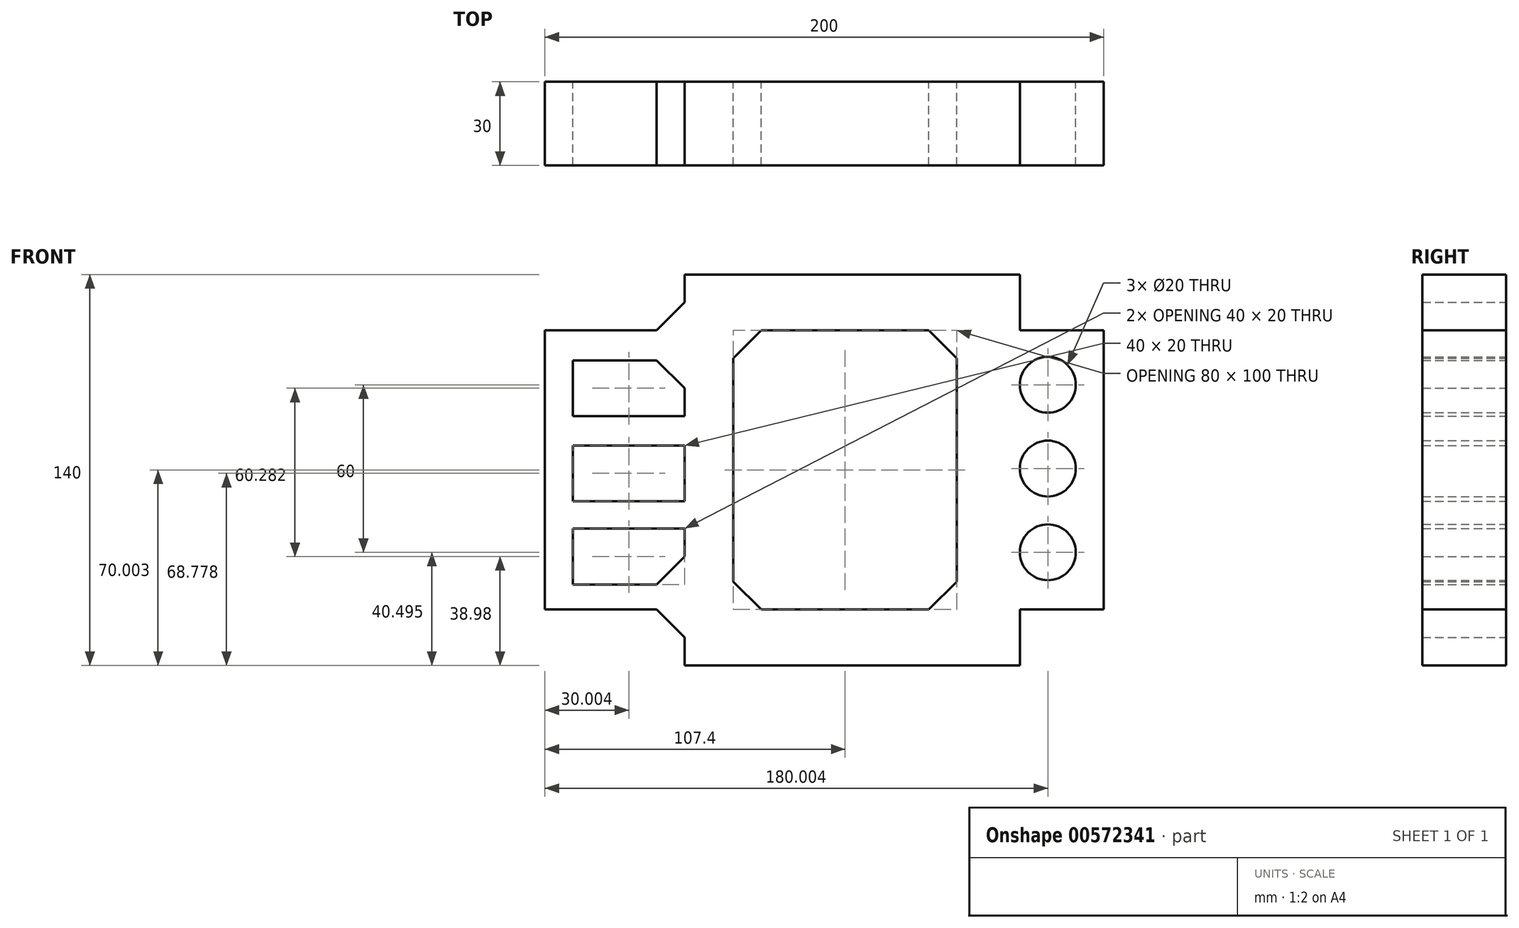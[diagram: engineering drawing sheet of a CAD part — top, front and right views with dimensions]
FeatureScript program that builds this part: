
annotation { "Feature Type Name" : "Feature", "Feature Type Description" : "" }
export const myFeature = defineFeature(function(context is Context, id is Id, definition is map)
    precondition{}
    {
        {
            var Q0;
            Q0=qCreatedBy(makeId("Front.planeOp"),FACE);
            var sketch = newSketch(context, id + "F0", { "sketchPlane" : qUnion([Q0])});
            skLineSegment(sketch, "E0.bottom", {"start": v(-33.54, -70.5) * mm, "end": v(66.46, -70.5) * mm});
            skLineSegment(sketch, "E0.top", {"start": v(-33.54, 69.5) * mm, "end": v(66.46, 69.5) * mm});
            skLineSegment(sketch, "E0.left", {"start": v(-43.54, -60.5) * mm, "end": v(-43.54, -60.5) * mm});
            skLineSegment(sketch, "E0.right", {"start": v(76.46, -60.5) * mm, "end": v(76.46, -60.5) * mm});
            skLineSegment(sketch, "E1.bottom", {"start": v(-83.54, 49.5) * mm, "end": v(-53.54, 49.5) * mm});
            skLineSegment(sketch, "E1.top", {"start": v(-83.54, -50.5) * mm, "end": v(-53.54, -50.5) * mm});
            skLineSegment(sketch, "E1.left", {"start": v(-93.54, 39.5) * mm, "end": v(-93.54, -40.5) * mm});
            skLineSegment(sketch, "E1.right", {"start": v(106.46, 39.5) * mm, "end": v(106.46, -40.5) * mm});
            skLineSegment(sketch, "E2.trimOffspring", {"start": v(-43.54, 59.5) * mm, "end": v(-43.54, 59.5) * mm});
            skLineSegment(sketch, "E3.trimOffspring", {"start": v(76.46, 59.5) * mm, "end": v(76.46, 59.5) * mm});
            skLineSegment(sketch, "E4.trimOffspring", {"start": v(86.46, 49.5) * mm, "end": v(96.46, 49.5) * mm});
            skLineSegment(sketch, "E5.trimOffspring", {"start": v(86.46, -50.5) * mm, "end": v(96.46, -50.5) * mm});
            skLineSegment(sketch, "E6.bottom", {"start": v(-16.14, 49.5) * mm, "end": v(43.86, 49.5) * mm});
            skLineSegment(sketch, "E6.top", {"start": v(-16.14, -50.5) * mm, "end": v(43.86, -50.5) * mm});
            skLineSegment(sketch, "E6.left", {"start": v(-26.14, 39.5) * mm, "end": v(-26.14, 24.5) * mm});
            skLineSegment(sketch, "E6.right", {"start": v(53.86, 39.5) * mm, "end": v(53.86, 24.5) * mm});
            skLineSegment(sketch, "E7.trimOffspring", {"start": v(-26.14, -0.5) * mm, "end": v(-26.14, -40.5) * mm});
            skLineSegment(sketch, "E8.trimOffspring", {"start": v(53.86, -0.5) * mm, "end": v(53.86, -40.5) * mm});
            skCircle(sketch, "E9", {"center": v(86.46, 29.98) * mm, "radius": 10 * mm});
            skCircle(sketch, "E10", {"center": v(86.46, -0.02) * mm, "radius": 10 * mm});
            skCircle(sketch, "E11", {"center": v(86.46, -30.02) * mm, "radius": 10 * mm});
            skLineSegment(sketch, "E12.bottom", {"start": v(-83.54, 38.75) * mm, "end": v(-53.54, 38.75) * mm});
            skLineSegment(sketch, "E12.top", {"start": v(-83.54, 18.75) * mm, "end": v(-43.54, 18.75) * mm});
            skLineSegment(sketch, "E12.left", {"start": v(-83.54, 38.75) * mm, "end": v(-83.54, 18.75) * mm});
            skLineSegment(sketch, "E12.right", {"start": v(-43.54, 28.75) * mm, "end": v(-43.54, 18.75) * mm});
            skLineSegment(sketch, "E13.bottom", {"start": v(-83.54, 8.27) * mm, "end": v(-43.54, 8.27) * mm});
            skLineSegment(sketch, "E13.top", {"start": v(-83.54, -11.73) * mm, "end": v(-43.54, -11.73) * mm});
            skLineSegment(sketch, "E13.left", {"start": v(-83.54, 8.27) * mm, "end": v(-83.54, -11.73) * mm});
            skLineSegment(sketch, "E13.right", {"start": v(-43.54, 8.27) * mm, "end": v(-43.54, -11.73) * mm});
            skLineSegment(sketch, "E14.bottom", {"start": v(-83.54, -21.53) * mm, "end": v(-43.54, -21.53) * mm});
            skLineSegment(sketch, "E14.top", {"start": v(-83.54, -41.53) * mm, "end": v(-53.54, -41.53) * mm});
            skLineSegment(sketch, "E14.left", {"start": v(-83.54, -21.53) * mm, "end": v(-83.54, -41.53) * mm});
            skLineSegment(sketch, "E14.right", {"start": v(-43.54, -21.53) * mm, "end": v(-43.54, -31.53) * mm});
            skPoint(sketch, "E15.visualSharp", {"position": v(-93.54, 49.5) * mm});
            skPoint(sketch, "E16.visualSharp", {"position": v(-43.54, 49.5) * mm});
            skPoint(sketch, "E17.visualSharp", {"position": v(-43.54, 69.5) * mm});
            skPoint(sketch, "E18.visualSharp", {"position": v(76.46, 69.5) * mm});
            skPoint(sketch, "E19.visualSharp", {"position": v(76.46, 49.5) * mm});
            skPoint(sketch, "E20.visualSharp", {"position": v(106.46, 49.5) * mm});
            skPoint(sketch, "E21.visualSharp", {"position": v(106.46, -50.5) * mm});
            skPoint(sketch, "E22.visualSharp", {"position": v(76.46, -50.5) * mm});
            skPoint(sketch, "E23.visualSharp", {"position": v(76.46, -70.5) * mm});
            skPoint(sketch, "E24.visualSharp", {"position": v(-43.54, -70.5) * mm});
            skPoint(sketch, "E25.visualSharp", {"position": v(-43.54, -50.5) * mm});
            skPoint(sketch, "E26.visualSharp", {"position": v(-93.54, -50.5) * mm});
            skPoint(sketch, "E27.visualSharp", {"position": v(-43.54, 38.75) * mm});
            skPoint(sketch, "E28.visualSharp", {"position": v(-43.54, -41.53) * mm});
            skPoint(sketch, "E29.visualSharp", {"position": v(53.86, 49.5) * mm});
            skPoint(sketch, "E30.visualSharp", {"position": v(-26.14, 49.5) * mm});
            skPoint(sketch, "E31.visualSharp", {"position": v(-26.14, -50.5) * mm});
            skPoint(sketch, "E32.visualSharp", {"position": v(53.86, -50.5) * mm});
            skLineSegment(sketch, "E33", {"start": v(76.46, 59.5) * mm, "end": v(76.46, 69.5) * mm});
            skLineSegment(sketch, "E34", {"start": v(66.46, 69.5) * mm, "end": v(76.46, 69.5) * mm});
            skLineSegment(sketch, "E35", {"start": v(76.46, 59.5) * mm, "end": v(76.46, 49.5) * mm});
            skLineSegment(sketch, "E36", {"start": v(76.46, 49.5) * mm, "end": v(86.46, 49.5) * mm});
            skLineSegment(sketch, "E37", {"start": v(106.46, 49.5) * mm, "end": v(106.46, 39.5) * mm});
            skLineSegment(sketch, "E38", {"start": v(106.46, 49.5) * mm, "end": v(96.46, 49.5) * mm});
            skLineSegment(sketch, "E39", {"start": v(106.46, -50.5) * mm, "end": v(96.46, -50.5) * mm});
            skLineSegment(sketch, "E40", {"start": v(106.46, -50.5) * mm, "end": v(106.46, -40.5) * mm});
            skLineSegment(sketch, "E41", {"start": v(86.46, -50.5) * mm, "end": v(76.46, -50.5) * mm});
            skLineSegment(sketch, "E42", {"start": v(76.46, -60.5) * mm, "end": v(76.46, -50.5) * mm});
            skLineSegment(sketch, "E43", {"start": v(76.46, -60.5) * mm, "end": v(76.46, -70.5) * mm});
            skLineSegment(sketch, "E44", {"start": v(66.46, -70.5) * mm, "end": v(76.46, -70.5) * mm});
            skLineSegment(sketch, "E45", {"start": v(-33.54, -70.5) * mm, "end": v(-43.54, -70.5) * mm});
            skLineSegment(sketch, "E46", {"start": v(-43.54, -60.5) * mm, "end": v(-43.54, -70.5) * mm});
            skLineSegment(sketch, "E47", {"start": v(-43.54, -60.5) * mm, "end": v(-53.54, -50.5) * mm});
            skLineSegment(sketch, "E48", {"start": v(-83.54, -50.5) * mm, "end": v(-93.54, -50.5) * mm});
            skLineSegment(sketch, "E49", {"start": v(-93.54, -50.5) * mm, "end": v(-93.54, -40.5) * mm});
            skLineSegment(sketch, "E50", {"start": v(-93.54, 39.5) * mm, "end": v(-93.54, 49.5) * mm});
            skLineSegment(sketch, "E51", {"start": v(-93.54, 49.5) * mm, "end": v(-83.54, 49.5) * mm});
            skLineSegment(sketch, "E52", {"start": v(-53.54, 49.5) * mm, "end": v(-43.54, 59.5) * mm});
            skLineSegment(sketch, "E53", {"start": v(-43.54, 59.5) * mm, "end": v(-43.54, 69.5) * mm});
            skLineSegment(sketch, "E54", {"start": v(-43.54, 69.5) * mm, "end": v(-33.54, 69.5) * mm});
            skLineSegment(sketch, "E55", {"start": v(-26.14, 39.5) * mm, "end": v(-16.14, 49.5) * mm});
            skLineSegment(sketch, "E56", {"start": v(53.86, 39.5) * mm, "end": v(43.86, 49.5) * mm});
            skLineSegment(sketch, "E57", {"start": v(-26.14, -40.5) * mm, "end": v(-16.14, -50.5) * mm});
            skLineSegment(sketch, "E58", {"start": v(43.86, -50.5) * mm, "end": v(53.86, -40.5) * mm});
            skLineSegment(sketch, "E59", {"start": v(-53.54, 38.75) * mm, "end": v(-43.54, 28.75) * mm});
            skLineSegment(sketch, "E60", {"start": v(-53.54, -41.53) * mm, "end": v(-43.54, -31.53) * mm});
            skLineSegment(sketch, "E61", {"start": v(-26.14, -0.5) * mm, "end": v(-26.14, 24.5) * mm});
            skLineSegment(sketch, "E62", {"start": v(53.86, -0.5) * mm, "end": v(53.86, 24.5) * mm});
            skSolve(sketch);
        }
        {
            var Q0;
            Q0 = qSketchRegion(id + "F0", true);
            extrude(context, id + "F1", {"entities" : qUnion([Q0]), "depth" : 30 * mm, "offsetDistance" : 25 * mm});
        }
    });
